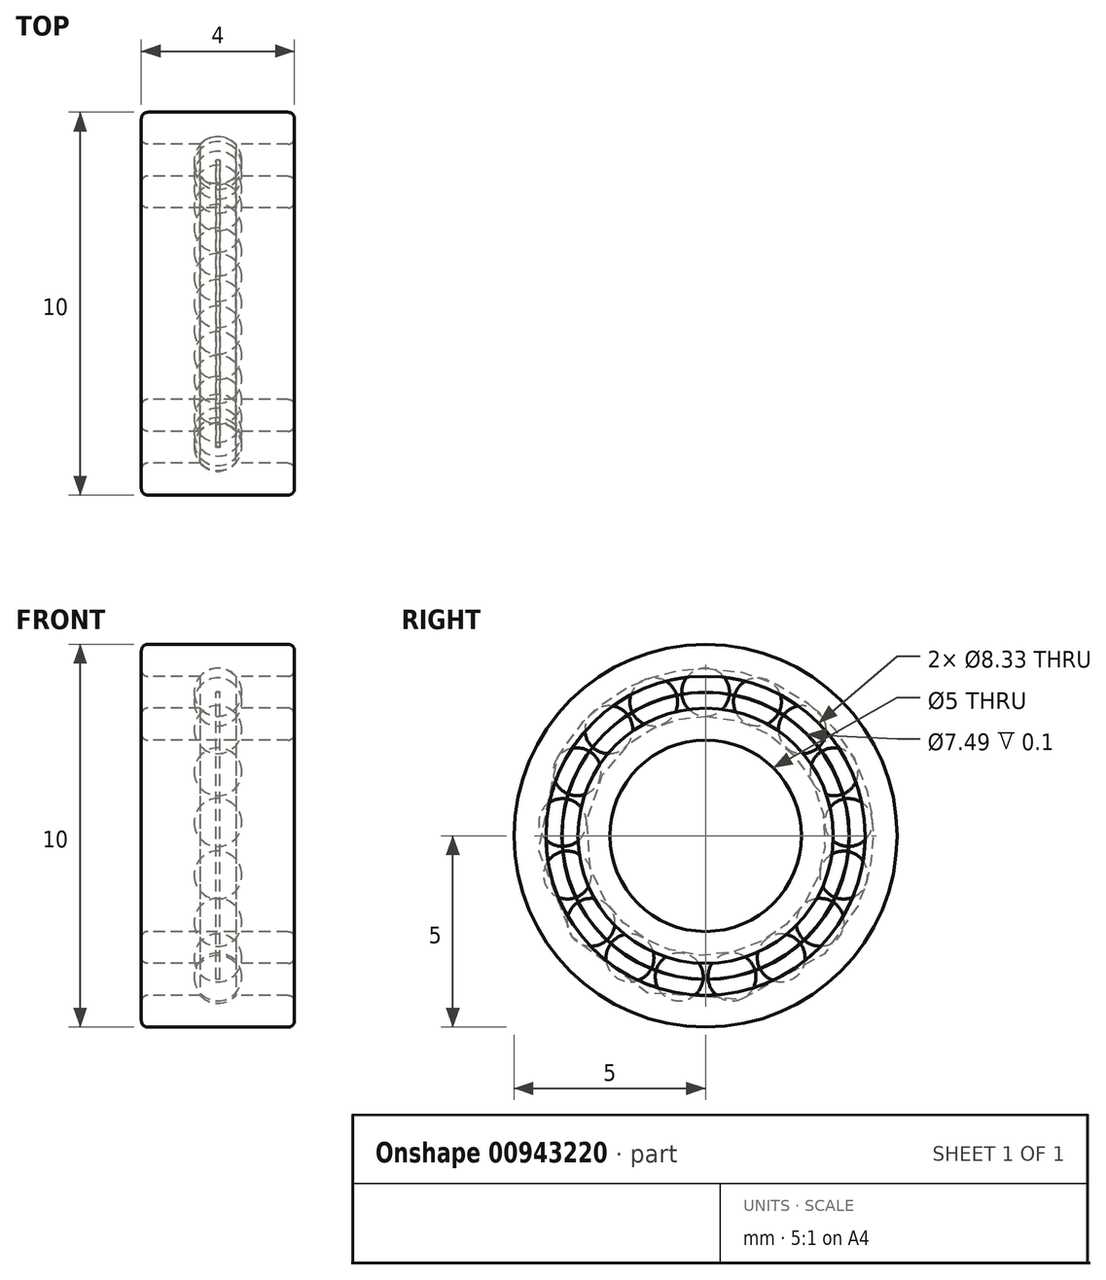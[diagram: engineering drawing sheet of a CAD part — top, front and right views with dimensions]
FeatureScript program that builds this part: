
annotation { "Feature Type Name" : "Feature", "Feature Type Description" : "" }
export const myFeature = defineFeature(function(context is Context, id is Id, definition is map)
    precondition{}
    {
        {
            var Q0;
            Q0=qCreatedBy(makeId("Front.planeOp"),FACE);
            var sketch = newSketch(context, id + "F0", { "sketchPlane" : qUnion([Q0])});
            skLineSegment(sketch, "E0", {"start": v(-2, 0) * mm, "end": v(2, 0) * mm, "construction": true});
            skLineSegment(sketch, "E1", {"start": v(-2, 0) * mm, "end": v(-2, 2.5) * mm, "construction": true});
            skLineSegment(sketch, "E2.MirrorCS", {"start": v(2, 0) * mm, "end": v(2, 2.5) * mm, "construction": true});
            skLineSegment(sketch, "E3", {"start": v(-1.83, 2.5) * mm, "end": v(1.83, 2.5) * mm});
            skLineSegment(sketch, "E4", {"start": v(-2, 2.67) * mm, "end": v(-2, 3.17) * mm});
            skLineSegment(sketch, "E5.MirrorCS", {"start": v(2, 2.67) * mm, "end": v(2, 3.17) * mm});
            skLineSegment(sketch, "E6", {"start": v(-1.83, 3.33) * mm, "end": v(0.83, 3.33) * mm});
            skLineSegment(sketch, "E7.MirrorCS", {"start": v(1.83, 3.33) * mm, "end": v(-0.83, 3.33) * mm});
            skLineSegment(sketch, "E8", {"start": v(-2, 0) * mm, "end": v(-2, 4.17) * mm, "construction": true});
            skLineSegment(sketch, "E9", {"start": v(-2, 4.33) * mm, "end": v(-2, 4.83) * mm});
            skLineSegment(sketch, "E10", {"start": v(-1.83, 5) * mm, "end": v(0, 5) * mm});
            skLineSegment(sketch, "E11.MirrorCS", {"start": v(1.83, 5) * mm, "end": v(0, 5) * mm});
            skLineSegment(sketch, "E12.MirrorCS", {"start": v(2, 4.33) * mm, "end": v(2, 4.83) * mm});
            skLineSegment(sketch, "E13", {"start": v(-1.83, 4.17) * mm, "end": v(0.83, 4.17) * mm});
            skLineSegment(sketch, "E14.MirrorCS", {"start": v(1.83, 4.17) * mm, "end": v(-0.83, 4.17) * mm});
            skPoint(sketch, "E15.visualSharp", {"position": v(2, 5) * mm});
            skArc(sketch, "E15.filletArc", {"start": v(2, 4.83) * mm, "mid": v(1.95, 4.95) * mm, "end": v(1.83, 5) * mm});
            skPoint(sketch, "E16.visualSharp", {"position": v(-2, 5) * mm});
            skArc(sketch, "E16.filletArc", {"start": v(-1.83, 5) * mm, "mid": v(-1.95, 4.95) * mm, "end": v(-2, 4.83) * mm});
            skPoint(sketch, "E17.visualSharp", {"position": v(-2, 2.5) * mm});
            skArc(sketch, "E17.filletArc", {"start": v(-2, 2.67) * mm, "mid": v(-1.95, 2.55) * mm, "end": v(-1.83, 2.5) * mm});
            skPoint(sketch, "E18.visualSharp", {"position": v(2, 2.5) * mm});
            skArc(sketch, "E18.filletArc", {"start": v(1.83, 2.5) * mm, "mid": v(1.95, 2.55) * mm, "end": v(2, 2.67) * mm});
            skPoint(sketch, "E19.visualSharp", {"position": v(-2, 4.17) * mm});
            skArc(sketch, "E19.filletArc", {"start": v(-2, 4.33) * mm, "mid": v(-1.95, 4.22) * mm, "end": v(-1.83, 4.17) * mm});
            skPoint(sketch, "E20.visualSharp", {"position": v(-2, 3.33) * mm});
            skArc(sketch, "E20.filletArc", {"start": v(-1.83, 3.33) * mm, "mid": v(-1.95, 3.28) * mm, "end": v(-2, 3.17) * mm});
            skPoint(sketch, "E21.visualSharp", {"position": v(2, 3.33) * mm});
            skArc(sketch, "E21.filletArc", {"start": v(2, 3.17) * mm, "mid": v(1.95, 3.28) * mm, "end": v(1.83, 3.33) * mm});
            skPoint(sketch, "E22.visualSharp", {"position": v(2, 4.17) * mm});
            skArc(sketch, "E22.filletArc", {"start": v(1.83, 4.17) * mm, "mid": v(1.95, 4.22) * mm, "end": v(2, 4.33) * mm});
            skCircle(sketch, "E23", {"center": v(0, 3.75) * mm, "radius": 0.62 * mm});
            skSolve(sketch);
        }
        {
            var Q0;
            Q0=makeQuery(id+"F0.imprint","IMPRINT",FACE,{"disambiguationData":[TD([[makeQuery(id+"F0.imprint","IMPRINT",EDGE,{"derivedFrom":sQuery(id+"F0.wireOp",EDGE,"E9")}),-1.0]])]});
            var Q1;
            Q1=makeQuery(id+"F0.imprint","IMPRINT",FACE,{"disambiguationData":[TD([[makeQuery(id+"F0.imprint","IMPRINT",EDGE,{"derivedFrom":sQuery(id+"F0.wireOp",EDGE,"E3")}),1.0]])]});
            var Q2;
            Q2=sQuery(id+"F0.wireOp",EDGE,"E0");
            revolve(context, id + "F1", {"surfaceOperationType" : NewSurfaceOperationType.NEW, "entities" : qUnion([Q0, Q1]), "axis" : qUnion([Q2]), "revolveType" : RevolveType.FULL});
        }
        {
            var Q0;
            Q0=qCreatedBy(makeId("Front.planeOp"),FACE);
            var sketch = newSketch(context, id + "F2", { "sketchPlane" : qUnion([Q0])});
            skArc(sketch, "E24", {"start": v(0.62, 3.75) * mm, "mid": v(0, 4.38) * mm, "end": v(-0.63, 3.75) * mm});
            skLineSegment(sketch, "E25", {"start": v(0, 3.75) * mm, "end": v(3.74, 3.75) * mm, "construction": true});
            skLineSegment(sketch, "E26", {"start": v(0, 3.75) * mm, "end": v(0, 23.25) * mm, "construction": true});
            skLineSegment(sketch, "E27.MirrorCS", {"start": v(0, 3.75) * mm, "end": v(-3.74, 3.75) * mm, "construction": true});
            skLineSegment(sketch, "E28", {"start": v(-0.63, 3.75) * mm, "end": v(0.62, 3.75) * mm});
            skSolve(sketch);
        }
        {
            var Q0;
            Q0=qSketchRegion(id+"F2",true);
            var Q1;
            Q1=sQuery(id+"F2.wireOp",EDGE,"E27.MirrorCS");
            revolve(context, id + "F3", {"surfaceOperationType" : NewSurfaceOperationType.NEW, "entities" : qUnion([Q0]), "axis" : qUnion([Q1]), "revolveType" : RevolveType.FULL});
        }
        {
            var Q0;
            Q0=qCreatedBy(makeId("Top.planeOp"),FACE);
            var sketch = newSketch(context, id + "F4", { "sketchPlane" : qUnion([Q0])});
            skLineSegment(sketch, "E29", {"start": v(0, 0) * mm, "end": v(16.63, 0) * mm, "construction": true});
            skSolve(sketch);
        }
        {
            var Q0;
            Q0=makeQuery(id+"F3.opRevolve","SWEPT_BODY",BODY,{"disambiguationData":[OSD([sQuery(id+"F2.wireOp",EDGE,"E24"),sQuery(id+"F2.wireOp",EDGE,"E28")])]});
            var Q1;
            Q1=sQuery(id+"F4.wireOp",EDGE,"E29");
            circularPattern(context, id + "F5", {"entities" : qUnion([Q0]), "axis" : qUnion([Q1]), "angle" : 360 * degree, "instanceCount" : 17, "equalSpace" : true});
        }
        {
            var Q0;
            Q0=qCreatedBy(makeId("Right.planeOp"),FACE);
            var sketch = newSketch(context, id + "F6", { "sketchPlane" : qUnion([Q0])});
            skCircle(sketch, "E30", {"center": v(0, 0) * mm, "radius": 3.75 * mm});
            skSolve(sketch);
        }
        {
            var Q0;
            Q0=qSketchRegion(id+"F6",true);
            extrude(context, id + "F7", {"entities" : qUnion([Q0]), "depth" : 0.1 * mm, "offsetDistance" : 25 * mm, "symmetric" : true});
        }
    });
